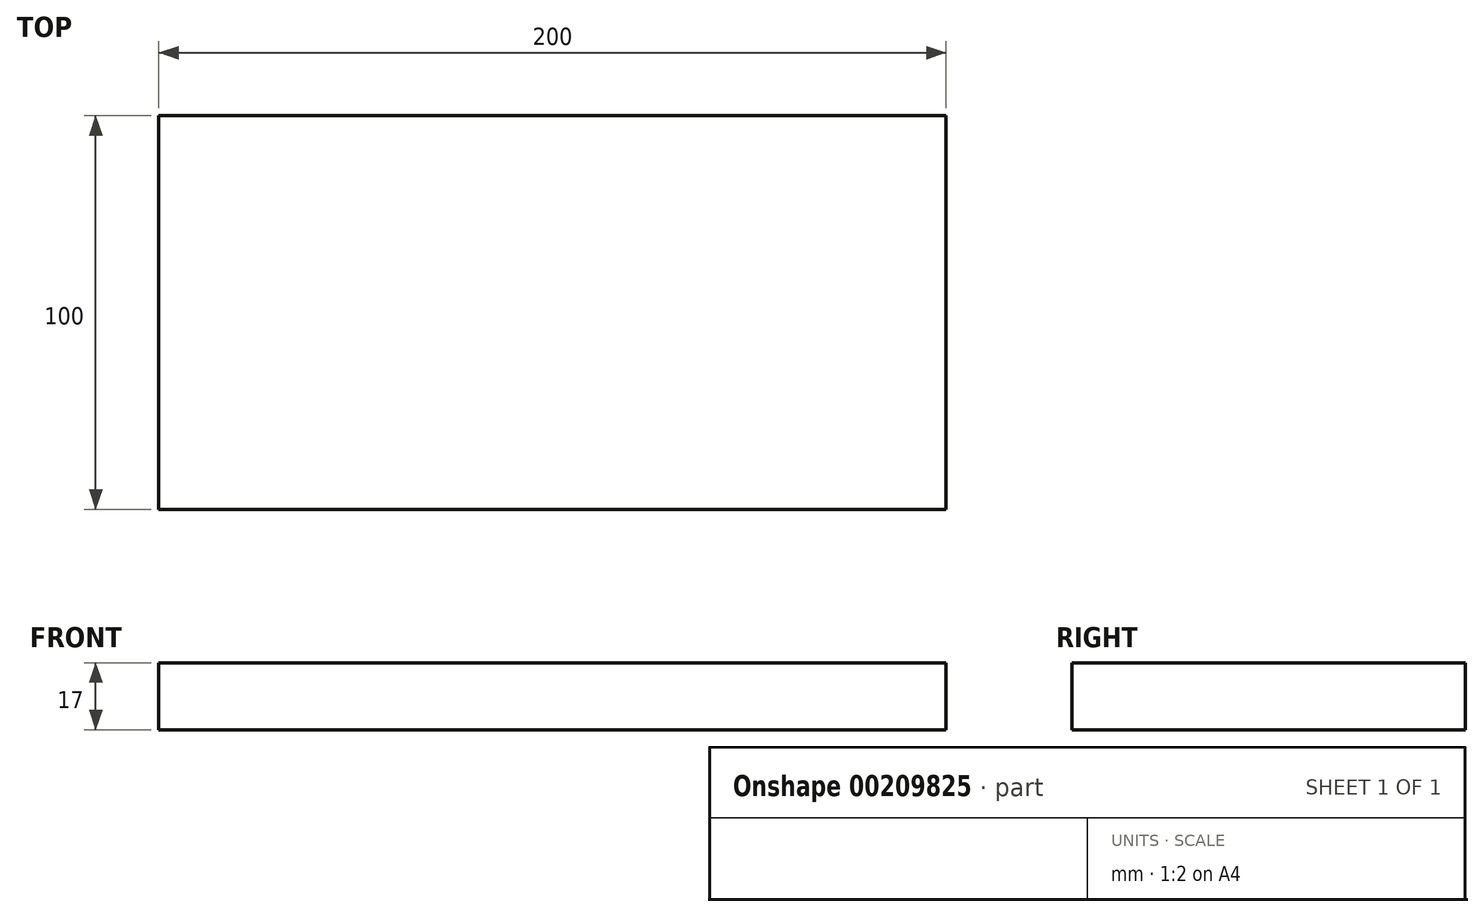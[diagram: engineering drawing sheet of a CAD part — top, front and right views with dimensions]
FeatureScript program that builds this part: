
annotation { "Feature Type Name" : "Feature", "Feature Type Description" : "" }
export const myFeature = defineFeature(function(context is Context, id is Id, definition is map)
    precondition{}
    {
        {
            var Q0;
            Q0=qCreatedBy(makeId("Top.planeOp"),FACE);
            var sketch = newSketch(context, id + "F0", { "sketchPlane" : qUnion([Q0])});
            skLineSegment(sketch, "E0.bottom", {"start": v(100, -50) * mm, "end": v(-100, -50) * mm});
            skLineSegment(sketch, "E0.top", {"start": v(100, 50) * mm, "end": v(-100, 50) * mm});
            skLineSegment(sketch, "E0.left", {"start": v(100, -50) * mm, "end": v(100, 50) * mm});
            skLineSegment(sketch, "E0.right", {"start": v(-100, -50) * mm, "end": v(-100, 50) * mm});
            skPoint(sketch, "E0.middle", {"position": v(0, 0) * mm});
            skSolve(sketch);
        }
        {
            var Q0;
            Q0=makeQuery(id+"F0.imprint","IMPRINT",FACE,{"disambiguationData":[TD([[makeQuery(id+"F0.imprint","IMPRINT",EDGE,{"derivedFrom":sQuery(id+"F0.wireOp",EDGE,"E0.bottom")}),-1.0]])]});
            extrude(context, id + "F1", {"entities" : qUnion([Q0]), "depth" : 17 * mm});
        }
    });
